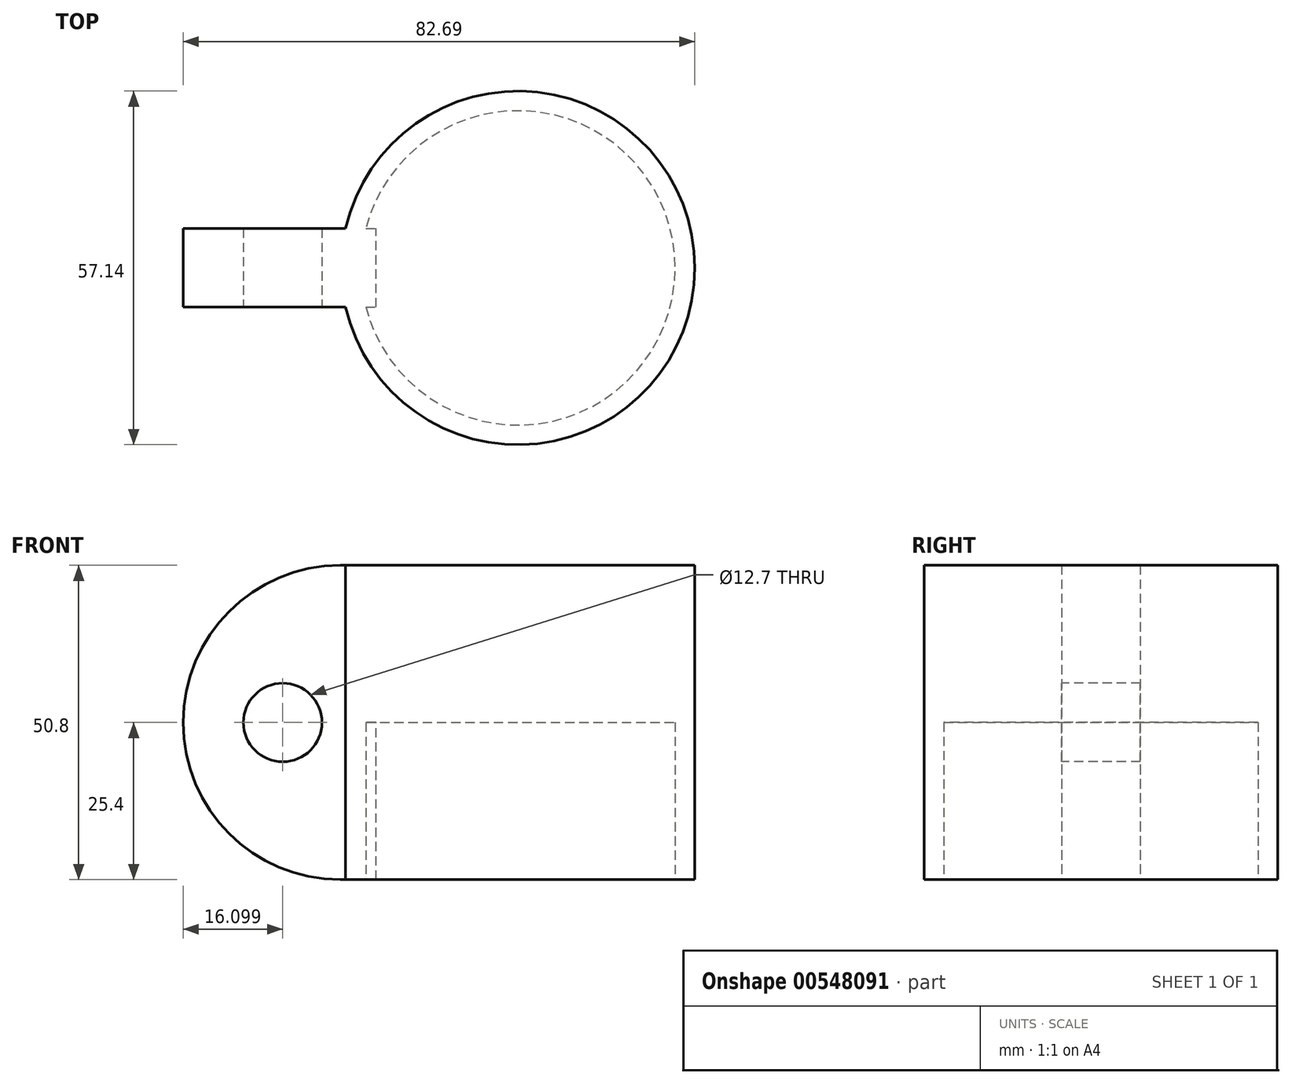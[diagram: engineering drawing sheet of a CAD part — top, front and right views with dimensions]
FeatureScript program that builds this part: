
annotation { "Feature Type Name" : "Feature", "Feature Type Description" : "" }
export const myFeature = defineFeature(function(context is Context, id is Id, definition is map)
    precondition{}
    {
        {
            var Q0;
            Q0=qCreatedBy(makeId("Top.planeOp"),FACE);
            var sketch = newSketch(context, id + "F0", { "sketchPlane" : qUnion([Q0])});
            skCircle(sketch, "E0", {"center": v(0, 0) * mm, "radius": 28.58 * mm});
            skSolve(sketch);
        }
        {
            var Q0;
            Q0=makeQuery(id+"F0.imprint","IMPRINT",FACE,{"disambiguationData":[TD([[makeQuery(id+"F0.imprint","IMPRINT",EDGE,{"derivedFrom":sQuery(id+"F0.wireOp",EDGE,"E0")}),1.0]])]});
            extrude(context, id + "F1", {"entities" : qUnion([Q0]), "depth" : 50.8 * mm, "offsetDistance" : 25.4 * mm});
        }
        {
            var Q0;
            Q0=makeQuery(id+"F1.opExtrude","CAP_FACE",FACE,{"disambiguationData":[OSD([sQuery(id+"F0.wireOp",EDGE,"E0")])],"isStart":true});
            var sketch = newSketch(context, id + "F2", { "sketchPlane" : qUnion([Q0])});
            skCircle(sketch, "E1", {"center": v(0, 0) * mm, "radius": 25.4 * mm});
            skSolve(sketch);
        }
        {
            var Q0;
            Q0=makeQuery(id+"F2.imprint","IMPRINT",FACE,{"disambiguationData":[TD([[makeQuery(id+"F2.imprint","IMPRINT",EDGE,{"derivedFrom":sQuery(id+"F2.wireOp",EDGE,"E1")}),1.0]])]});
            extrude(context, id + "F3", {"entities" : qUnion([Q0]), "operationType" : NewBodyOperationType.REMOVE, "oppositeDirection" : true, "depth" : 25.4 * mm, "offsetDistance" : 25.4 * mm});
        }
        {
            var Q0;
            Q0=qCreatedBy(makeId("Front.planeOp"),FACE);
            var sketch = newSketch(context, id + "F4", { "sketchPlane" : qUnion([Q0])});
            skLineSegment(sketch, "E2.bottom", {"start": v(-28.72, 0) * mm, "end": v(-22.92, 0) * mm});
            skLineSegment(sketch, "E2.top", {"start": v(-28.72, 50.8) * mm, "end": v(-22.92, 50.8) * mm});
            skLineSegment(sketch, "E2.right", {"start": v(-22.92, 0) * mm, "end": v(-22.92, 50.8) * mm});
            skArc(sketch, "E3", {"start": v(-28.72, 50.8) * mm, "mid": v(-54.12, 25.4) * mm, "end": v(-28.72, 0) * mm});
            skSolve(sketch);
        }
        {
            var Q0;
            Q0=makeQuery(id+"F4.imprint","IMPRINT",FACE,{"disambiguationData":[TD([[makeQuery(id+"F4.imprint","IMPRINT",EDGE,{"derivedFrom":sQuery(id+"F4.wireOp",EDGE,"E2.bottom")}),1.0]])]});
            extrude(context, id + "F5", {"entities" : qUnion([Q0]), "operationType" : NewBodyOperationType.ADD, "depth" : 6.35 * mm, "offsetDistance" : 25.4 * mm, "hasSecondDirection" : true, "secondDirectionOppositeDirection" : true, "secondDirectionDepth" : 6.35 * mm});
        }
        {
            var Q0;
            {var subQ0=sQuery(id+"F4.wireOp",EDGE,"E2.bottom");var subQ1=sQuery(id+"F0.wireOp",EDGE,"E0");var subQ2=sQuery(id+"F4.wireOp",EDGE,"E3");var subQ3=sQuery(id+"F4.wireOp",EDGE,"E2.top");Q0=makeQuery(id+"F5.boolean.opBoolean","SPLIT",FACE,{"disambiguationData":[TD([makeQuery(id+"F1.opExtrude","SWEPT_FACE",FACE,{"disambiguationData":[OSD([subQ1])]})])],"derivedFrom":makeQuery(id+"F5.opExtrude","CAP_FACE",FACE,{"disambiguationData":[OSD([subQ0,subQ3,sQuery(id+"F4.wireOp",EDGE,"E2.right"),subQ2])],"isStart":false})});}
            var sketch = newSketch(context, id + "F6", { "sketchPlane" : qUnion([Q0])});
            skCircle(sketch, "E4", {"center": v(-38.02, 25.4) * mm, "radius": 6.35 * mm});
            skSolve(sketch);
        }
        {
            var Q0;
            Q0 = qSketchRegion(id + "F6", true);
            extrude(context, id + "F7", {"entities" : qUnion([Q0]), "operationType" : NewBodyOperationType.REMOVE, "oppositeDirection" : true, "depth" : 25.4 * mm, "offsetDistance" : 25.4 * mm});
        }
        {
            var Q0;
            Q0=qCreatedBy(makeId("Front.planeOp"),FACE);
            var sketch = newSketch(context, id + "F8", { "sketchPlane" : qUnion([Q0])});
            skLineSegment(sketch, "E5", {"start": v(0, -12.95) * mm, "end": v(0, 52.58) * mm});
            skSolve(sketch);
        }
    });
